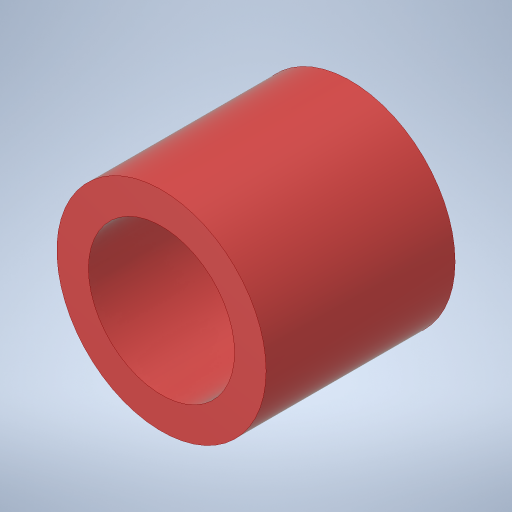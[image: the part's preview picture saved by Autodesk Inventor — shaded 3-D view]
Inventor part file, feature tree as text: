
AUTODESK INVENTOR PART (.ipt)
format: ipt  version: 2023.4 (Build 274418000, 418)  size: 235,520 bytes
history: native  units: in
note: dims shown in document units (in); Inventor stores cm internally (conversion verified against a paired STEP export)
features: extrude x1
ambient origin geometry x8: Origin, YZ Plane, XZ Plane, XY Plane, X Axis, Y Axis, Z Axis, Center Point
bodies: Solid1 (feature_tree)
feature tree (1):
  extrude  "Extrusion1"  TaperAngle=0.0deg  [1 undecoded]
note: 1 required parameter value undecoded (feature->parameter linkage not recoverable at this tier; creation-order binding heuristic only, values carry confidence <= 0.55)
